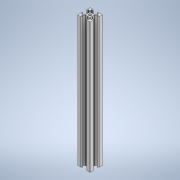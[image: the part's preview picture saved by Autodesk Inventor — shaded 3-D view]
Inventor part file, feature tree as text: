
AUTODESK INVENTOR PART (.ipt)
format: ipt  version: 2021 (Build 250183000, 183)  size: 236,032 bytes
history: native  units: mm
features: sketch x3, extrude x2, fillet x2, other x1, pattern_circular x1, hole x1, projected_geometry x1
ambient origin geometry x8: Origin, YZ Plane, XZ Plane, XY Plane, X Axis, Y Axis, Z Axis, Center Point
bodies: Body1 (feature_tree)
feature tree (11):
  other  "實體1"
  extrude  "擠出1"  Depth=20.0mm
  extrude  "擠出2"  Depth=20.0mm
  fillet  "圓角1"  Radius=210.0mm
  pattern_circular  "環形陣列1"  [2 undecoded]
  hole  "孔1"  [1 undecoded]
  fillet  "圓角2"  Radius=6.2mm
  sketch  "草圖1"
  sketch  "草圖2"
  projected_geometry  "投影迴路1"
  sketch  "草圖3"
note: 3 required parameter values undecoded (feature->parameter linkage not recoverable at this tier; creation-order binding heuristic only, values carry confidence <= 0.55)
